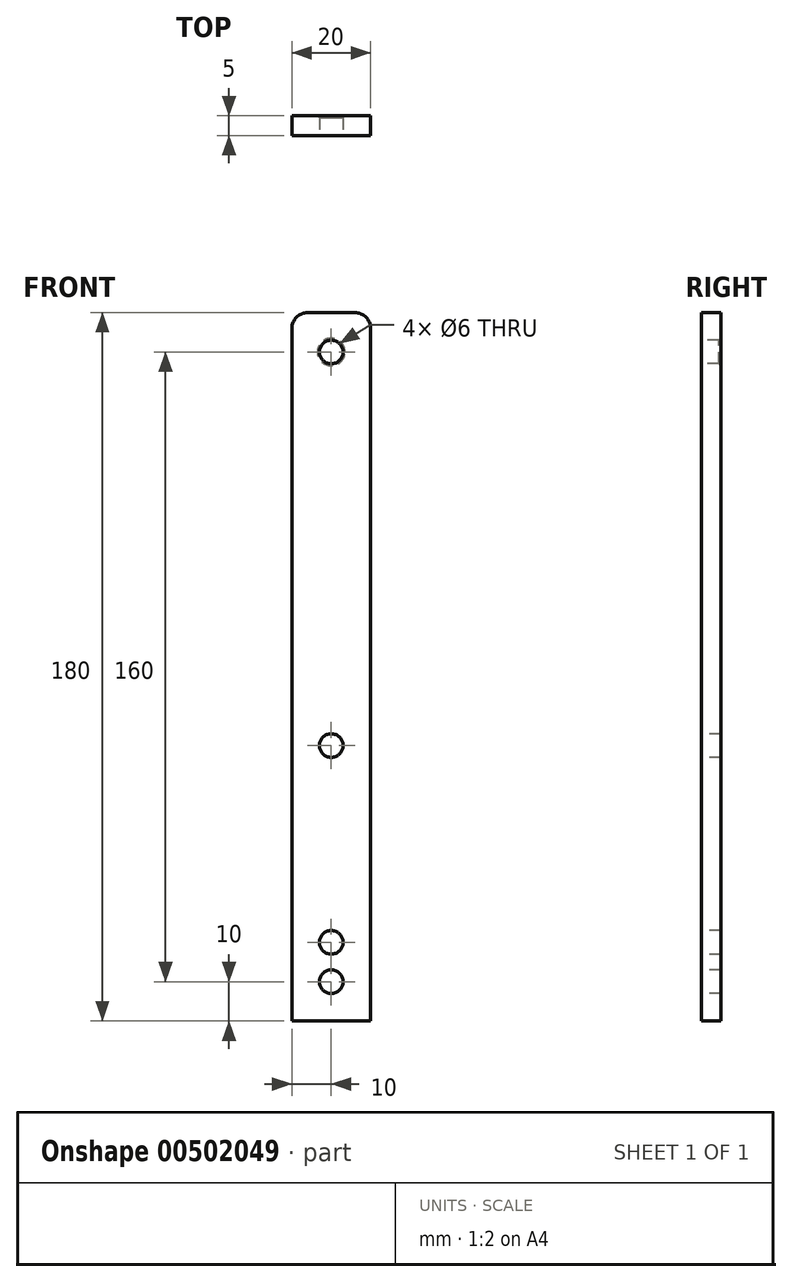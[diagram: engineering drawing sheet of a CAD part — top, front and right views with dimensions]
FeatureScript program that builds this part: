
annotation { "Feature Type Name" : "Feature", "Feature Type Description" : "" }
export const myFeature = defineFeature(function(context is Context, id is Id, definition is map)
    precondition{}
    {
        {
            var Q0;
            Q0=qCreatedBy(makeId("Front.planeOp"),FACE);
            var sketch = newSketch(context, id + "F0", { "sketchPlane" : qUnion([Q0])});
            skLineSegment(sketch, "E0.bottom", {"start": v(0, 0) * mm, "end": v(20, 0) * mm});
            skLineSegment(sketch, "E0.top", {"start": v(0, 180) * mm, "end": v(20, 180) * mm});
            skLineSegment(sketch, "E0.left", {"start": v(0, 0) * mm, "end": v(0, 180) * mm});
            skLineSegment(sketch, "E0.right", {"start": v(20, 0) * mm, "end": v(20, 180) * mm});
            skSolve(sketch);
        }
        {
            var Q0;
            Q0 = qSketchRegion(id + "F0", true);
            extrude(context, id + "F1", {"entities" : qUnion([Q0]), "depth" : 5 * mm});
        }
        {
            var Q0;
            Q0=makeQuery(id+"F1.opExtrude","CAP_FACE",FACE,{"disambiguationData":[OSD([sQuery(id+"F0.wireOp",EDGE,"E0.bottom"),sQuery(id+"F0.wireOp",EDGE,"E0.top"),sQuery(id+"F0.wireOp",EDGE,"E0.left"),sQuery(id+"F0.wireOp",EDGE,"E0.right")])],"isStart":false});
            var sketch = newSketch(context, id + "F2", { "sketchPlane" : qUnion([Q0])});
            skCircle(sketch, "E1", {"center": v(10, 170) * mm, "radius": 3 * mm});
            skSolve(sketch);
        }
        {
            var Q0;
            Q0 = qSketchRegion(id + "F2", true);
            extrude(context, id + "F3", {"entities" : qUnion([Q0]), "operationType" : NewBodyOperationType.REMOVE, "endBound" : BoundingType.THROUGH_ALL, "oppositeDirection" : true, "depth" : 25 * mm});
        }
        {
            var Q0;
            Q0=makeQuery(id+"F1.opExtrude","CAP_FACE",FACE,{"disambiguationData":[OSD([sQuery(id+"F0.wireOp",EDGE,"E0.bottom"),sQuery(id+"F0.wireOp",EDGE,"E0.top"),sQuery(id+"F0.wireOp",EDGE,"E0.left"),sQuery(id+"F0.wireOp",EDGE,"E0.right")])],"isStart":false});
            var sketch = newSketch(context, id + "F4", { "sketchPlane" : qUnion([Q0])});
            skLineSegment(sketch, "E2", {"start": v(10, 170) * mm, "end": v(10, 70) * mm});
            skSolve(sketch);
        }
        {
            var Q0;
            Q0=sQuery(id+"F4.wireOp",VERTEX,"E2.end");
            var Q1;
            Q1=makeQuery(id+"F1.opExtrude","SWEPT_BODY",BODY,{"disambiguationData":[OSD([sQuery(id+"F0.wireOp",EDGE,"E0.bottom"),sQuery(id+"F0.wireOp",EDGE,"E0.top"),sQuery(id+"F0.wireOp",EDGE,"E0.left"),sQuery(id+"F0.wireOp",EDGE,"E0.right")])]});
            hole(context, id + "F5", {"style" : HoleStyle.SIMPLE, "endStyle" : HoleEndStyle.THROUGH, "holeDiameter" : 6 * mm, "isTappedThrough" : true, "tappedDepth" : 12 * mm, "tapClearance" : 3, "locations" : qUnion([Q0]), "scope" : qUnion([Q1])});
        }
        {
            var Q0;
            Q0=makeQuery(id+"F1.opExtrude","CAP_FACE",FACE,{"disambiguationData":[OSD([sQuery(id+"F0.wireOp",EDGE,"E0.bottom"),sQuery(id+"F0.wireOp",EDGE,"E0.top"),sQuery(id+"F0.wireOp",EDGE,"E0.left"),sQuery(id+"F0.wireOp",EDGE,"E0.right")])],"isStart":false});
            var sketch = newSketch(context, id + "F6", { "sketchPlane" : qUnion([Q0])});
            skLineSegment(sketch, "E3", {"start": v(10, 0) * mm, "end": v(10, 10) * mm});
            skLineSegment(sketch, "E4", {"start": v(10, 10) * mm, "end": v(10, 20) * mm});
            skSolve(sketch);
        }
        {
            var Q0;
            Q0=sQuery(id+"F6.wireOp",VERTEX,"E4.start");
            var Q1;
            Q1=sQuery(id+"F6.wireOp",VERTEX,"E4.end");
            var Q2;
            Q2=makeQuery(id+"F1.opExtrude","SWEPT_BODY",BODY,{"disambiguationData":[OSD([sQuery(id+"F0.wireOp",EDGE,"E0.bottom"),sQuery(id+"F0.wireOp",EDGE,"E0.top"),sQuery(id+"F0.wireOp",EDGE,"E0.left"),sQuery(id+"F0.wireOp",EDGE,"E0.right")])]});
            hole(context, id + "F7", {"style" : HoleStyle.SIMPLE, "endStyle" : HoleEndStyle.THROUGH, "holeDiameter" : 6 * mm, "isTappedThrough" : true, "tappedDepth" : 12 * mm, "tapClearance" : 3, "locations" : qUnion([Q0, Q1]), "scope" : qUnion([Q2])});
        }
        {
            var Q0;
            Q0=makeQuery(id+"F3.boolean.opBoolean","COPY",EDGE,{"derivedFrom":makeQuery(id+"F3.opExtrude","CAP_EDGE",EDGE,{"disambiguationData":[OSD([sQuery(id+"F2.wireOp",EDGE,"E1")])],"isStart":true})});
            var Q1;
            Q1=makeQuery(id+"F3.boolean.opBoolean","INTERSECT",EDGE,{"derivedFrom":[makeQuery(id+"F1.opExtrude","CAP_FACE",FACE,{"disambiguationData":[OSD([sQuery(id+"F0.wireOp",EDGE,"E0.bottom"),sQuery(id+"F0.wireOp",EDGE,"E0.top"),sQuery(id+"F0.wireOp",EDGE,"E0.left"),sQuery(id+"F0.wireOp",EDGE,"E0.right")])],"isStart":true}),makeQuery(id+"F3.opExtrude","SWEPT_FACE",FACE,{"disambiguationData":[OSD([sQuery(id+"F2.wireOp",EDGE,"E1")])]})]});
            var Q2;
            Q2=makeQuery(id+"F5.hole-0.boolean.opBoolean","INTERSECT",EDGE,{"derivedFrom":[makeQuery(id+"F1.opExtrude","CAP_FACE",FACE,{"disambiguationData":[OSD([sQuery(id+"F0.wireOp",EDGE,"E0.bottom"),sQuery(id+"F0.wireOp",EDGE,"E0.top"),sQuery(id+"F0.wireOp",EDGE,"E0.left"),sQuery(id+"F0.wireOp",EDGE,"E0.right")])],"isStart":true}),makeQuery(id+"F5.hole-0.opRevolve","SWEPT_FACE",FACE,{"disambiguationData":[OSD([sQuery(id+"F5.hole-0.sketch.wireOp",EDGE,"core_line_2")])]})]});
            var Q3;
            Q3=makeQuery(id+"F5.hole-0.boolean.opBoolean","COPY",EDGE,{"derivedFrom":makeQuery(id+"F5.hole-0.opRevolve","SWEPT_EDGE",EDGE,{"disambiguationData":[OSD([sQuery(id+"F5.hole-0.sketch.wireOp",EDGE,"core_line_2"),sQuery(id+"F5.hole-0.sketch.wireOp",EDGE,"core_line_3")])]})});
            var Q4;
            Q4=makeQuery(id+"F7.hole-1.boolean.opBoolean","COPY",EDGE,{"derivedFrom":makeQuery(id+"F7.hole-1.opRevolve","SWEPT_EDGE",EDGE,{"disambiguationData":[OSD([sQuery(id+"F7.hole-1.sketch.wireOp",EDGE,"core_line_2"),sQuery(id+"F7.hole-1.sketch.wireOp",EDGE,"core_line_3")])]})});
            var Q5;
            Q5=makeQuery(id+"F7.hole-1.boolean.opBoolean","INTERSECT",EDGE,{"derivedFrom":[makeQuery(id+"F1.opExtrude","CAP_FACE",FACE,{"disambiguationData":[OSD([sQuery(id+"F0.wireOp",EDGE,"E0.bottom"),sQuery(id+"F0.wireOp",EDGE,"E0.top"),sQuery(id+"F0.wireOp",EDGE,"E0.left"),sQuery(id+"F0.wireOp",EDGE,"E0.right")])],"isStart":true}),makeQuery(id+"F7.hole-1.opRevolve","SWEPT_FACE",FACE,{"disambiguationData":[OSD([sQuery(id+"F7.hole-1.sketch.wireOp",EDGE,"core_line_2")])]})]});
            var Q6;
            Q6=makeQuery(id+"F7.hole-0.boolean.opBoolean","COPY",EDGE,{"derivedFrom":makeQuery(id+"F7.hole-0.opRevolve","SWEPT_EDGE",EDGE,{"disambiguationData":[OSD([sQuery(id+"F7.hole-0.sketch.wireOp",EDGE,"core_line_2"),sQuery(id+"F7.hole-0.sketch.wireOp",EDGE,"core_line_3")])]})});
            var Q7;
            Q7=makeQuery(id+"F7.hole-0.boolean.opBoolean","INTERSECT",EDGE,{"derivedFrom":[makeQuery(id+"F1.opExtrude","CAP_FACE",FACE,{"disambiguationData":[OSD([sQuery(id+"F0.wireOp",EDGE,"E0.bottom"),sQuery(id+"F0.wireOp",EDGE,"E0.top"),sQuery(id+"F0.wireOp",EDGE,"E0.left"),sQuery(id+"F0.wireOp",EDGE,"E0.right")])],"isStart":true}),makeQuery(id+"F7.hole-0.opRevolve","SWEPT_FACE",FACE,{"disambiguationData":[OSD([sQuery(id+"F7.hole-0.sketch.wireOp",EDGE,"core_line_2")])]})]});
            chamfer(context, id + "F8", {"entities" : qUnion([Q0, Q1, Q2, Q3, Q4, Q5, Q6, Q7]), "width" : 0.5 * mm, "tangentPropagation" : true});
        }
        {
            var Q0;
            Q0=makeQuery(id+"F1.opExtrude","SWEPT_EDGE",EDGE,{"disambiguationData":[OSD([sQuery(id+"F0.wireOp",EDGE,"E0.top"),sQuery(id+"F0.wireOp",EDGE,"E0.right")])]});
            var Q1;
            Q1=makeQuery(id+"F1.opExtrude","SWEPT_EDGE",EDGE,{"disambiguationData":[OSD([sQuery(id+"F0.wireOp",EDGE,"E0.top"),sQuery(id+"F0.wireOp",EDGE,"E0.left")])]});
            fillet(context, id + "F9", {"entities" : qUnion([Q0, Q1]), "radius" : 4 * mm, "tangentPropagation" : true, "allowEdgeOverflow" : false});
        }
    });
